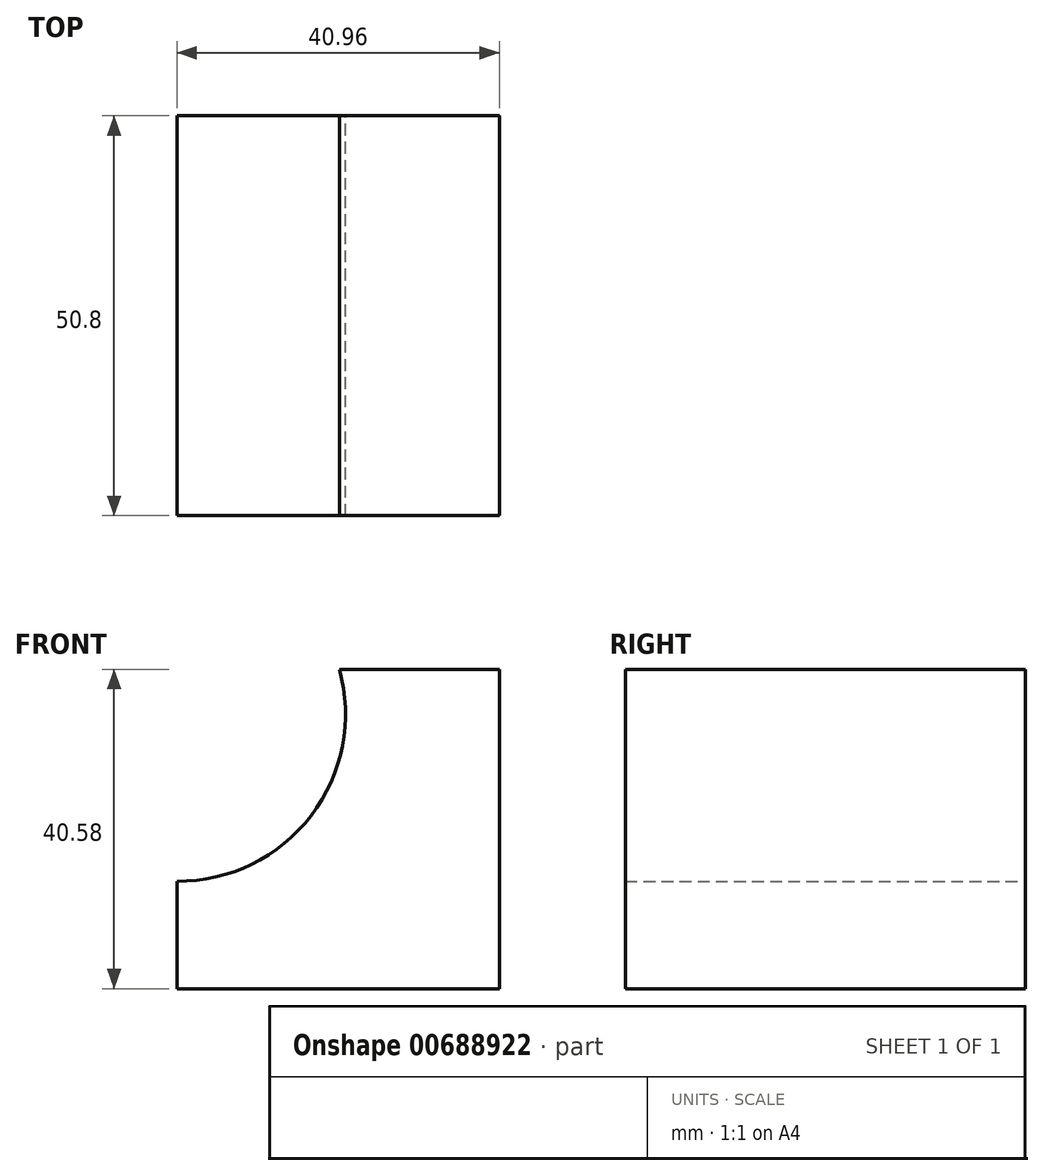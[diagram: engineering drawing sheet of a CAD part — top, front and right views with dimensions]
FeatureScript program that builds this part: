
annotation { "Feature Type Name" : "Feature", "Feature Type Description" : "" }
export const myFeature = defineFeature(function(context is Context, id is Id, definition is map)
    precondition{}
    {
        {
            var Q0;
            Q0=qCreatedBy(makeId("Front.planeOp"),FACE);
            var sketch = newSketch(context, id + "F0", { "sketchPlane" : qUnion([Q0])});
            skLineSegment(sketch, "E0", {"start": v(-40.96, 0) * mm, "end": v(0, 0) * mm});
            skLineSegment(sketch, "E1", {"start": v(0, 0) * mm, "end": v(0, 40.58) * mm});
            skLineSegment(sketch, "E2", {"start": v(0, 40.58) * mm, "end": v(-20.34, 40.58) * mm});
            skLineSegment(sketch, "E3", {"start": v(-40.96, 0) * mm, "end": v(-40.96, 13.65) * mm});
            skArc(sketch, "E4", {"start": v(-40.96, 13.65) * mm, "mid": v(-23.93, 21.97) * mm, "end": v(-20.34, 40.58) * mm});
            skSolve(sketch);
        }
        {
            var Q0;
            Q0 = qSketchRegion(id + "F0", true);
            extrude(context, id + "F1", {"entities" : qUnion([Q0]), "depth" : 50.8 * mm, "offsetDistance" : 25.4 * mm});
        }
    });
